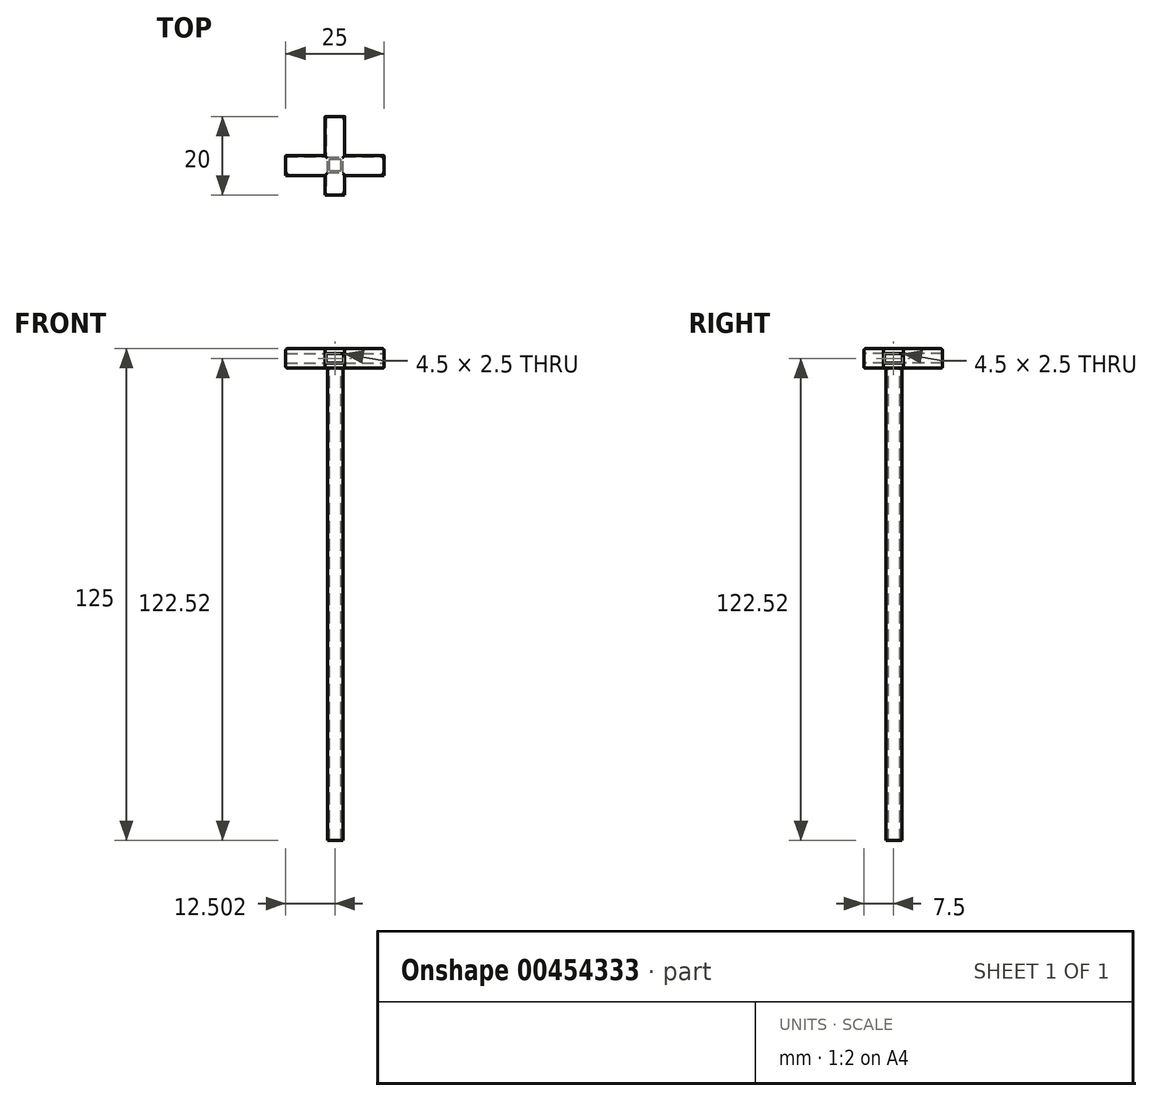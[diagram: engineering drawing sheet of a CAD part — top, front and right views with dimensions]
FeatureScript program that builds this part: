
annotation { "Feature Type Name" : "Feature", "Feature Type Description" : "" }
export const myFeature = defineFeature(function(context is Context, id is Id, definition is map)
    precondition{}
    {
        {
            var Q0;
            Q0=qCreatedBy(makeId("Top.planeOp"),FACE);
            var sketch = newSketch(context, id + "F0", { "sketchPlane" : qUnion([Q0])});
            skLineSegment(sketch, "E0", {"start": v(-12.16, 3.81) * mm, "end": v(-12.16, -1.19) * mm});
            skLineSegment(sketch, "E1", {"start": v(-12.16, -1.19) * mm, "end": v(-2.16, -1.19) * mm});
            skLineSegment(sketch, "E2", {"start": v(-2.16, -1.19) * mm, "end": v(-2.16, -6.19) * mm});
            skLineSegment(sketch, "E3", {"start": v(-2.16, -6.19) * mm, "end": v(2.84, -6.19) * mm});
            skLineSegment(sketch, "E4", {"start": v(2.84, -6.19) * mm, "end": v(2.84, -1.19) * mm});
            skLineSegment(sketch, "E5", {"start": v(2.84, -1.19) * mm, "end": v(12.84, -1.19) * mm});
            skLineSegment(sketch, "E6", {"start": v(12.84, -1.19) * mm, "end": v(12.84, 3.81) * mm});
            skLineSegment(sketch, "E7", {"start": v(12.84, 3.81) * mm, "end": v(2.84, 3.81) * mm});
            skLineSegment(sketch, "E8", {"start": v(2.84, 3.81) * mm, "end": v(2.84, 13.81) * mm});
            skLineSegment(sketch, "E9", {"start": v(2.84, 13.81) * mm, "end": v(-2.16, 13.81) * mm});
            skLineSegment(sketch, "E10", {"start": v(-2.16, 13.81) * mm, "end": v(-2.16, 3.81) * mm});
            skLineSegment(sketch, "E11", {"start": v(-2.16, 3.81) * mm, "end": v(-12.16, 3.81) * mm});
            skSolve(sketch);
        }
        {
            var Q0;
            Q0 = qSketchRegion(id + "F0", true);
            extrude(context, id + "F1", {"entities" : qUnion([Q0]), "depth" : 5 * mm});
        }
        {
            var Q0;
            Q0=makeQuery(id+"F1.opExtrude","CAP_FACE",FACE,{"disambiguationData":[OSD([sQuery(id+"F0.wireOp",EDGE,"E0"),sQuery(id+"F0.wireOp",EDGE,"E1"),sQuery(id+"F0.wireOp",EDGE,"E2"),sQuery(id+"F0.wireOp",EDGE,"E3"),sQuery(id+"F0.wireOp",EDGE,"E4"),sQuery(id+"F0.wireOp",EDGE,"E5"),sQuery(id+"F0.wireOp",EDGE,"E6"),sQuery(id+"F0.wireOp",EDGE,"E7"),sQuery(id+"F0.wireOp",EDGE,"E8"),sQuery(id+"F0.wireOp",EDGE,"E9"),sQuery(id+"F0.wireOp",EDGE,"E10"),sQuery(id+"F0.wireOp",EDGE,"E11")])],"isStart":false});
            var Q1;
            Q1=makeQuery(id+"F1.opExtrude","CAP_FACE",FACE,{"disambiguationData":[OSD([sQuery(id+"F0.wireOp",EDGE,"E0"),sQuery(id+"F0.wireOp",EDGE,"E1"),sQuery(id+"F0.wireOp",EDGE,"E2"),sQuery(id+"F0.wireOp",EDGE,"E3"),sQuery(id+"F0.wireOp",EDGE,"E4"),sQuery(id+"F0.wireOp",EDGE,"E5"),sQuery(id+"F0.wireOp",EDGE,"E6"),sQuery(id+"F0.wireOp",EDGE,"E7"),sQuery(id+"F0.wireOp",EDGE,"E8"),sQuery(id+"F0.wireOp",EDGE,"E9"),sQuery(id+"F0.wireOp",EDGE,"E10"),sQuery(id+"F0.wireOp",EDGE,"E11")])],"isStart":true});
            fillet(context, id + "F2", {"entities" : qUnion([Q0, Q1]), "radius" : 0.5 * mm, "tangentPropagation" : true, "allowEdgeOverflow" : false});
        }
        {
            var Q0;
            Q0=qCreatedBy(makeId("Right.planeOp"),FACE);
            var sketch = newSketch(context, id + "F3", { "sketchPlane" : qUnion([Q0])});
            skLineSegment(sketch, "E12.bottom", {"start": v(3.56, 3.77) * mm, "end": v(-0.94, 3.77) * mm});
            skLineSegment(sketch, "E12.top", {"start": v(3.56, 1.27) * mm, "end": v(-0.94, 1.27) * mm});
            skLineSegment(sketch, "E12.left", {"start": v(3.56, 3.77) * mm, "end": v(3.56, 1.27) * mm});
            skLineSegment(sketch, "E12.right", {"start": v(-0.94, 3.77) * mm, "end": v(-0.94, 1.27) * mm});
            skSolve(sketch);
        }
        {
            var Q0;
            Q0 = qSketchRegion(id + "F3", true);
            extrude(context, id + "F4", {"entities" : qUnion([Q0]), "operationType" : NewBodyOperationType.REMOVE, "endBound" : BoundingType.SYMMETRIC, "oppositeDirection" : true, "depth" : 50 * mm});
        }
        {
            var Q0;
            Q0=qCreatedBy(makeId("Front.planeOp"),FACE);
            var sketch = newSketch(context, id + "F5", { "sketchPlane" : qUnion([Q0])});
            skLineSegment(sketch, "E13.bottom", {"start": v(2.6, 3.77) * mm, "end": v(-1.9, 3.77) * mm});
            skLineSegment(sketch, "E13.top", {"start": v(2.6, 1.27) * mm, "end": v(-1.9, 1.27) * mm});
            skLineSegment(sketch, "E13.left", {"start": v(2.6, 3.77) * mm, "end": v(2.6, 1.27) * mm});
            skLineSegment(sketch, "E13.right", {"start": v(-1.9, 3.77) * mm, "end": v(-1.9, 1.27) * mm});
            skSolve(sketch);
        }
        {
            var Q0;
            Q0 = qSketchRegion(id + "F5", true);
            extrude(context, id + "F6", {"entities" : qUnion([Q0]), "operationType" : NewBodyOperationType.REMOVE, "endBound" : BoundingType.SYMMETRIC, "oppositeDirection" : true, "depth" : 50 * mm});
        }
        {
            var Q0;
            Q0=qCreatedBy(makeId("Top.planeOp"),FACE);
            var sketch = newSketch(context, id + "F7", { "sketchPlane" : qUnion([Q0])});
            skLineSegment(sketch, "E14.bottom", {"start": v(-1.58, -0.54) * mm, "end": v(2.42, -0.54) * mm});
            skLineSegment(sketch, "E14.top", {"start": v(-1.58, 3.46) * mm, "end": v(2.42, 3.46) * mm});
            skLineSegment(sketch, "E14.left", {"start": v(-1.58, -0.54) * mm, "end": v(-1.58, 3.46) * mm});
            skLineSegment(sketch, "E14.right", {"start": v(2.42, -0.54) * mm, "end": v(2.42, 3.46) * mm});
            skLineSegment(sketch, "E15.bottom", {"start": v(-1.07, 0) * mm, "end": v(1.93, 0) * mm});
            skLineSegment(sketch, "E15.top", {"start": v(-1.07, 3) * mm, "end": v(1.93, 3) * mm});
            skLineSegment(sketch, "E15.left", {"start": v(-1.07, 0) * mm, "end": v(-1.07, 3) * mm});
            skLineSegment(sketch, "E15.right", {"start": v(1.93, 0) * mm, "end": v(1.93, 3) * mm});
            skSolve(sketch);
        }
        {
            var Q0;
            Q0=makeQuery(id+"F7.imprint","IMPRINT",FACE,{"disambiguationData":[TD([[makeQuery(id+"F7.imprint","IMPRINT",EDGE,{"derivedFrom":sQuery(id+"F7.wireOp",EDGE,"E14.bottom")}),1.0]])]});
            extrude(context, id + "F8", {"entities" : qUnion([Q0]), "operationType" : NewBodyOperationType.ADD, "oppositeDirection" : true, "depth" : 120 * mm});
        }
    });
